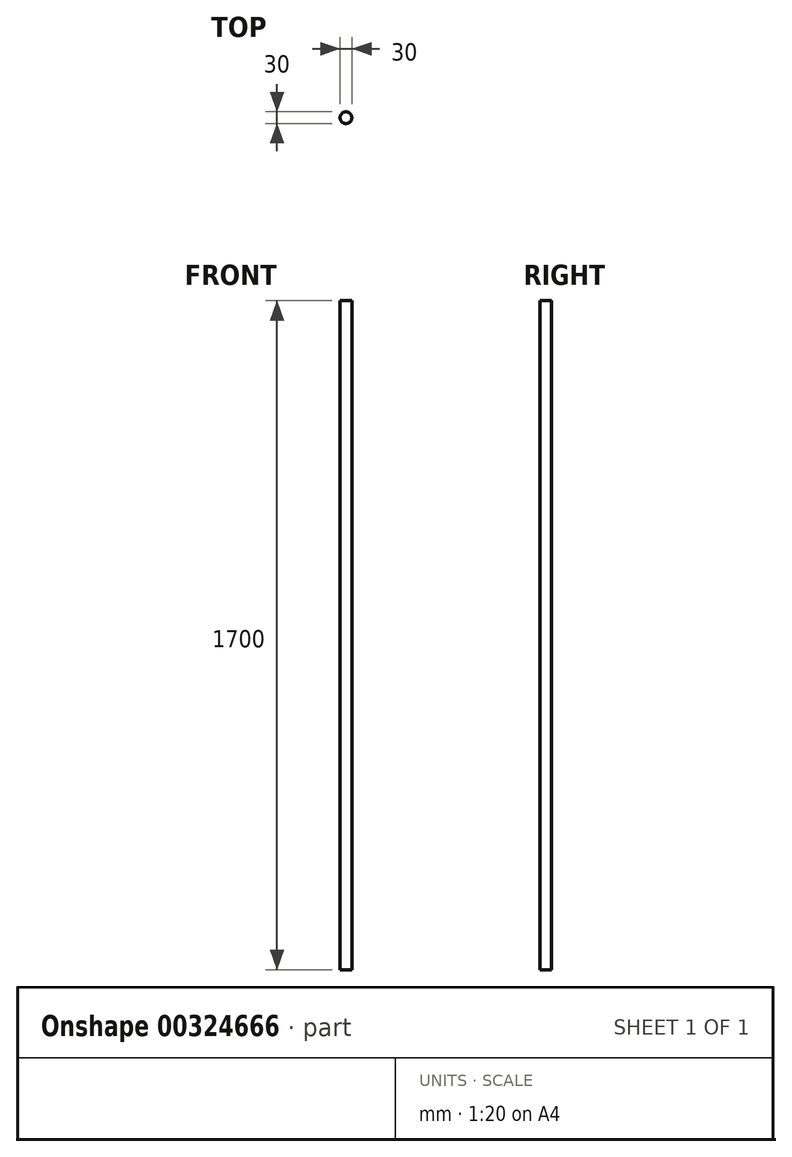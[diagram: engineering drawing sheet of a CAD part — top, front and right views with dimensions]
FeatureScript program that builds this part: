
annotation { "Feature Type Name" : "Feature", "Feature Type Description" : "" }
export const myFeature = defineFeature(function(context is Context, id is Id, definition is map)
    precondition{}
    {
        {
            var Q0;
            Q0=qCreatedBy(makeId("Top.planeOp"),FACE);
            var sketch = newSketch(context, id + "F0", { "sketchPlane" : qUnion([Q0])});
            skCircle(sketch, "E0", {"center": v(0, 0) * mm, "radius": 15 * mm});
            skSolve(sketch);
        }
        {
            var Q0;
            Q0 = qSketchRegion(id + "F0", true);
            extrude(context, id + "F1", {"entities" : qUnion([Q0]), "depth" : 1700 * mm});
        }
    });
